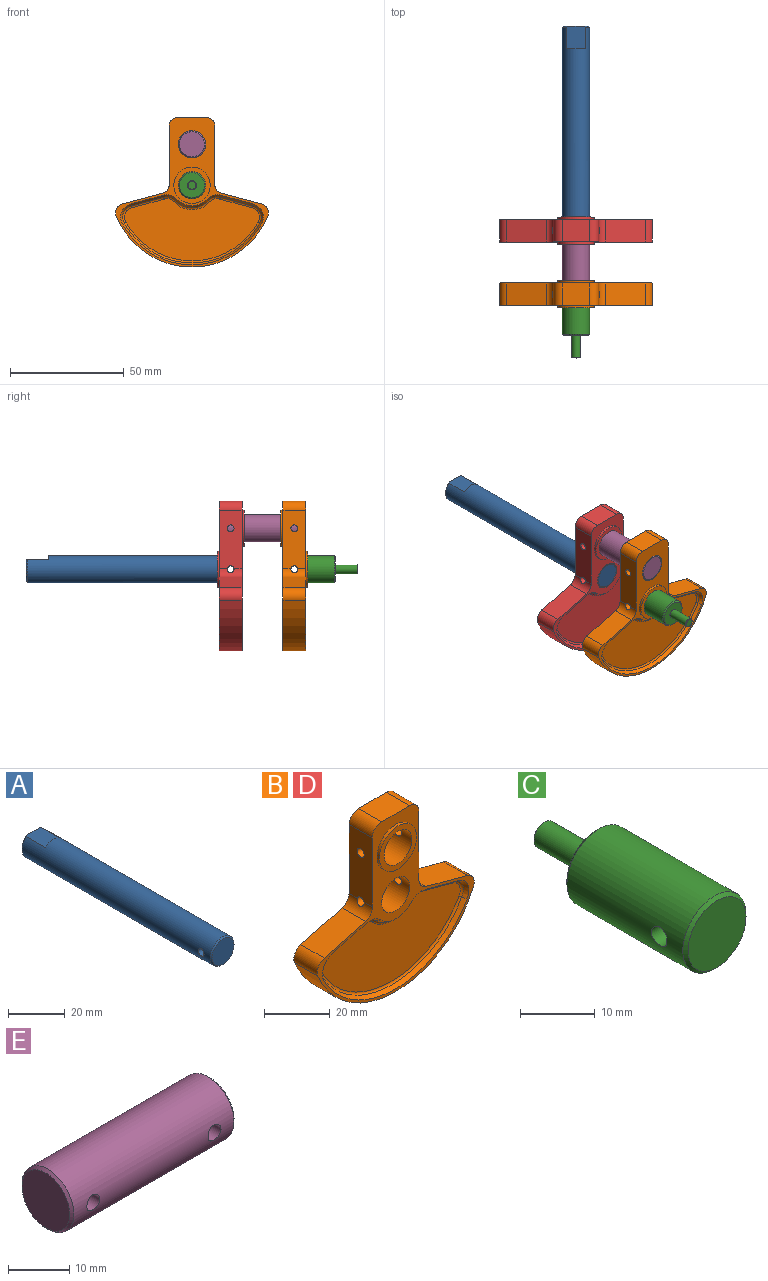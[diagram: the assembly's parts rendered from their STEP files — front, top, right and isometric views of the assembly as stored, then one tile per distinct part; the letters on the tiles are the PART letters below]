
ASSEMBLY  parts=5 mates=4
PART A: 8 faces, bbox 12x95x12 mm
  f0: cylinder r=6mm len=94mm, axis (0,1,0), area 3447.1mm2, adj f3,f4,f5,f6,f7
  f1: plane 11x10mm, normal (0,1,0), area 90.7mm2, adj f3,f6
  f2: plane 11x11mm, normal (0,-1,0), area 95mm2, adj f5
  f3: plane 10x7.94mm, normal (0,0,1), area 79mm2, adj f0,f1,f4,f6
  f4: plane 7.94x1.5mm, normal (0,1,0), area 8.2mm2, adj f0,f3
  f5: cone r=5.5mm half-angle=45deg, axis (0,1,0), area 25.5mm2, adj f0,f2
  f6: cone r=6mm half-angle=45deg, axis (0,-1,0), area 20.1mm2, adj f0,f1,f3
  f7: cylinder r=1.5mm len=12mm, axis (-1,0,0), area 111.3mm2, adj f0
PART B: 66 faces, bbox 67.3x12x67.1 mm
  f0: cylinder r=4mm len=10mm, axis (0,1,0), area 47.5mm2, adj f6,f7,f14,f15,f62
  f1: cylinder r=4mm len=10mm, axis (0,1,0), area 47.5mm2, adj f11,f12,f14,f15,f63
  f2: cylinder r=6mm len=12mm, axis (0,1,0), area 400.4mm2, adj f15,f17,f64,f65
  f3: cylinder r=6mm len=12mm, axis (0,1,0), area 400.4mm2, adj f14,f19,f62,f63
  f4: plane 12x10mm, normal (0,0,1), area 120mm2, adj f5,f13,f14,f15
  f5: cylinder r=4mm len=10mm, axis (0,1,0), area 62.8mm2, adj f4,f6,f14,f15
  f6: plane 25.61x10mm, normal (-1,0,0), area 246.7mm2, adj f0,f5,f14,f15,f62,f64
  f7: plane 17.7x10mm, normal (-0.26,0,0.97), area 183.3mm2, adj f0,f8,f14,f15
  f8: cylinder r=4mm len=10mm, axis (0,1,0), area 67.8mm2, adj f7,f9,f14,f15
  f9: cylinder r=36mm len=66.67mm, axis (0,1,0), area 852.2mm2, adj f8,f10,f14,f15
  f10: cylinder r=4mm len=10mm, axis (0,1,0), area 67.8mm2, adj f9,f11,f14,f15
  f11: plane 17.7x10mm, normal (0.26,0,0.97), area 183.3mm2, adj f1,f10,f14,f15
  f12: plane 25.61x10mm, normal (1,0,0), area 246.7mm2, adj f1,f13,f14,f15,f63,f65
  f13: cylinder r=4mm len=10mm, axis (0,1,0), area 62.8mm2, adj f4,f12,f14,f15
  f14: plane 67.26x66mm, normal (0,-1,0), area 580.6mm2, adj f0,f1,f3,f4,f5,f6,f7,f8
  f15: plane 67.26x66mm, normal (0,1,0), area 580.6mm2, adj f0,f1,f2,f4,f5,f6,f7,f8
  f16: cylinder r=8mm len=16mm, axis (0,1,0), area 50.3mm2, adj f14,f17
  f17: plane 16x16mm, normal (0,-1,0), area 88mm2, adj f2,f16
  f18: cylinder r=8mm len=16mm, axis (0,-1,0), area 50.3mm2, adj f15,f19
  f19: plane 16x16mm, normal (0,1,0), area 88mm2, adj f3,f18
  f20: plane 59.28x27.34mm, normal (0,1,0), area 1159.8mm2, adj f52,f53,f54,f55,f56,f57,f58,f59
  f21: plane 59.28x27.34mm, normal (0,-1,0), area 1159.8mm2, adj f42,f43,f44,f45,f46,f47,f48,f49
  f22: plane 14.44x4.65mm, normal (0.22,0.5,-0.84), area 25.5mm2, adj f15,f23,f24,f58
  f23: cone r=7mm half-angle=30deg, axis (0,-1,0), area 0.1mm2, adj f15,f22,f25,f56
  f24: cone r=6mm half-angle=30deg, axis (0,1,0), area 17.5mm2, adj f15,f22,f26,f60
  f25: cone r=6mm half-angle=30deg, axis (0,1,0), area 10.6mm2, adj f15,f23,f27,f54
  f26: cone r=35mm half-angle=30deg, axis (0,1,0), area 127.6mm2, adj f15,f24,f28,f61
  f27: cone r=11mm half-angle=30deg, axis (0,-1,0), area 26.9mm2, adj f15,f25,f29,f52
  f28: cone r=6mm half-angle=30deg, axis (0,1,0), area 17.5mm2, adj f15,f26,f30,f59
  f29: cone r=6mm half-angle=30deg, axis (0,1,0), area 10.6mm2, adj f15,f27,f31,f53
  f30: plane 14.44x4.65mm, normal (-0.22,0.5,-0.84), area 25.5mm2, adj f15,f28,f31,f57
  f31: cone r=7mm half-angle=30deg, axis (0,-1,0), area 0.1mm2, adj f15,f29,f30,f55
  f32: plane 14.44x4.65mm, normal (-0.22,-0.5,-0.84), area 25.5mm2, adj f14,f33,f34,f46
  f33: cone r=4mm half-angle=30deg, axis (0,-1,0), area 17.5mm2, adj f14,f32,f35,f48
  f34: cone r=5mm half-angle=30deg, axis (0,1,0), area 0.1mm2, adj f14,f32,f36,f44
  f35: cone r=33mm half-angle=30deg, axis (0,-1,0), area 127.6mm2, adj f14,f33,f37,f50
  f36: cone r=4mm half-angle=30deg, axis (0,-1,0), area 10.6mm2, adj f14,f34,f38,f42
  f37: cone r=4mm half-angle=30deg, axis (0,-1,0), area 17.5mm2, adj f14,f35,f39,f51
  f38: cone r=9mm half-angle=30deg, axis (0,1,0), area 26.9mm2, adj f14,f36,f40,f43
  f39: plane 14.44x4.65mm, normal (0.22,-0.5,-0.84), area 25.5mm2, adj f14,f37,f41,f49
  f40: cone r=4mm half-angle=30deg, axis (0,-1,0), area 10.6mm2, adj f14,f38,f41,f45
  f41: cone r=5mm half-angle=30deg, axis (0,1,0), area 0.1mm2, adj f14,f39,f40,f47
  f42: torus R=4.27mm, axis (0,-1,0), area 5.5mm2, adj f21,f36,f43,f44
  f43: torus R=10.73mm, axis (0,-1,0), area 17.7mm2, adj f21,f38,f42,f45
  f44: torus R=6.73mm, axis (0,-1,0), area 0.1mm2, adj f21,f34,f42,f46
  f45: torus R=4.27mm, axis (0,-1,0), area 5.5mm2, adj f21,f40,f43,f47
  f46: cylinder r=1mm len=14.44mm, axis (0.97,0,-0.26), area 15.4mm2, adj f21,f32,f44,f48
  f47: torus R=6.73mm, axis (0,-1,0), area 0.1mm2, adj f21,f41,f45,f49
  f48: torus R=4.27mm, axis (0,-1,0), area 9mm2, adj f21,f33,f46,f50
  f49: cylinder r=1mm len=14.44mm, axis (-0.97,0,-0.26), area 15.4mm2, adj f21,f39,f47,f51
  f50: torus R=33.27mm, axis (0,-1,0), area 75.3mm2, adj f21,f35,f48,f51
  f51: torus R=4.27mm, axis (0,-1,0), area 9mm2, adj f21,f37,f49,f50
  f52: torus R=10.73mm, axis (0,-1,0), area 17.7mm2, adj f20,f27,f53,f54
  f53: torus R=4.27mm, axis (0,-1,0), area 5.5mm2, adj f20,f29,f52,f55
  f54: torus R=4.27mm, axis (0,-1,0), area 5.5mm2, adj f20,f25,f52,f56
  f55: torus R=6.73mm, axis (0,-1,0), area 0.1mm2, adj f20,f31,f53,f57
  f56: torus R=6.73mm, axis (0,-1,0), area 0.1mm2, adj f20,f23,f54,f58
  f57: cylinder r=1mm len=14.44mm, axis (-0.97,0,0.26), area 15.4mm2, adj f20,f30,f55,f59
  f58: cylinder r=1mm len=14.44mm, axis (0.97,0,0.26), area 15.4mm2, adj f20,f22,f56,f60
  f59: torus R=4.27mm, axis (0,-1,0), area 9mm2, adj f20,f28,f57,f61
  f60: torus R=4.27mm, axis (0,-1,0), area 9mm2, adj f20,f24,f58,f61
  f61: torus R=33.27mm, axis (0,-1,0), area 75.3mm2, adj f20,f26,f59,f60
  f62: cylinder r=1.5mm len=4.67mm, axis (-1,0,0), area 39.8mm2, adj f0,f3,f6
  f63: cylinder r=1.5mm len=4.67mm, axis (-1,0,0), area 39.8mm2, adj f1,f3,f12
  f64: cylinder r=1.5mm len=4.19mm, axis (-1,0,0), area 38.6mm2, adj f2,f6
  f65: cylinder r=1.5mm len=4.19mm, axis (-1,0,0), area 38.6mm2, adj f2,f12
PART C: 9 faces, bbox 12x33x12 mm
  f0: cylinder r=6mm len=22mm, axis (0,1,0), area 815.1mm2, adj f5,f6,f7
  f1: plane 11x11mm, normal (0,-1,0), area 95mm2, adj f7
  f2: plane 11x11mm, normal (0,1,0), area 82.5mm2, adj f3,f6
  f3: cylinder r=2mm len=9.75mm, axis (0,-1,0), area 122.5mm2, adj f2,f8
  f4: plane 3.5x3.5mm, normal (0,1,0), area 9.6mm2, adj f8
  f5: cylinder r=1.5mm len=12mm, axis (1,0,0), area 111.3mm2, adj f0
  f6: cone r=6mm half-angle=45deg, axis (0,-1,0), area 25.5mm2, adj f0,f2
  f7: cone r=5.5mm half-angle=45deg, axis (0,1,0), area 25.5mm2, adj f0,f1
  f8: cone r=2mm half-angle=45deg, axis (0,-1,0), area 4.2mm2, adj f3,f4
PART D: same geometry as B
PART E: 7 faces, bbox 38x12x12 mm
  f0: cylinder r=6mm len=37mm, axis (1,0,0), area 1366.3mm2, adj f3,f4,f5,f6
  f1: plane 11x11mm, normal (1,0,0), area 95mm2, adj f5
  f2: plane 11x11mm, normal (-1,0,0), area 95mm2, adj f6
  f3: cylinder r=1.5mm len=12mm, axis (0,1,0), area 111.3mm2, adj f0
  f4: cylinder r=1.5mm len=12mm, axis (0,1,0), area 111.3mm2, adj f0
  f5: cone r=5.5mm half-angle=45deg, axis (-1,0,0), area 25.5mm2, adj f0,f1
  f6: cone r=6mm half-angle=45deg, axis (1,0,0), area 25.5mm2, adj f0,f2
PLACE A t=(27.76,112.56,8.6)mm
PLACE B rot(axis=(0,0,1),180deg) t=(27.76,-5.44,8.6)mm
PLACE C rot(axis=(0,0,1),180deg) t=(27.76,-5.44,8.6)mm
PLACE D t=(27.76,22.56,8.6)mm
PLACE E rot(axis=(0.58,0.58,0.58),120deg) t=(27.76,8.56,26.6)mm
MATE fastened E.f0 <-> D.f2  axis (0,1,0) through (27.76,27.56,26.6)mm
MATE fastened A.f0 <-> D.f3  axis (0,-1,0) through (27.76,17.56,8.6)mm
MATE fastened B.f3 <-> C.f0  axis (0,1,0) through (27.76,-0.44,8.6)mm
MATE fastened B.f2 <-> E.f0  axis (0,-1,0) through (27.76,-10.44,26.6)mm
